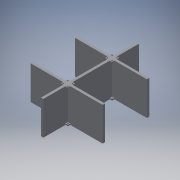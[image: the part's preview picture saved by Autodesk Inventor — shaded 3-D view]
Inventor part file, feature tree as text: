
AUTODESK INVENTOR PART (.ipt)
format: ipt  version: 2019 (Build 230136000, 136)  size: 273,408 bytes
history: native  units: mm
features: other x3, extrude x3, sketch x2, mirror x1, projected_geometry x1
ambient origin geometry x8: Origin, YZ Plane, XZ Plane, XY Plane, X Axis, Y Axis, Z Axis, Center Point
bodies: Body1 (feature_tree)
feature tree (10):
  other  "крепление-стенки"
  other  "Твердое тело1"
  sketch  "Эскиз1"
  extrude  "Выдавливание1"  Depth=120.0mm
  other  "РабПлоскость1"
  extrude  "Выдавливание2"  Depth=4.0mm
  mirror  "Зеркальное отражение1"
  extrude  "Выдавливание3"  Depth=4.0mm
  sketch  "Эскиз2"
  projected_geometry  "Спроецированная петля1"
